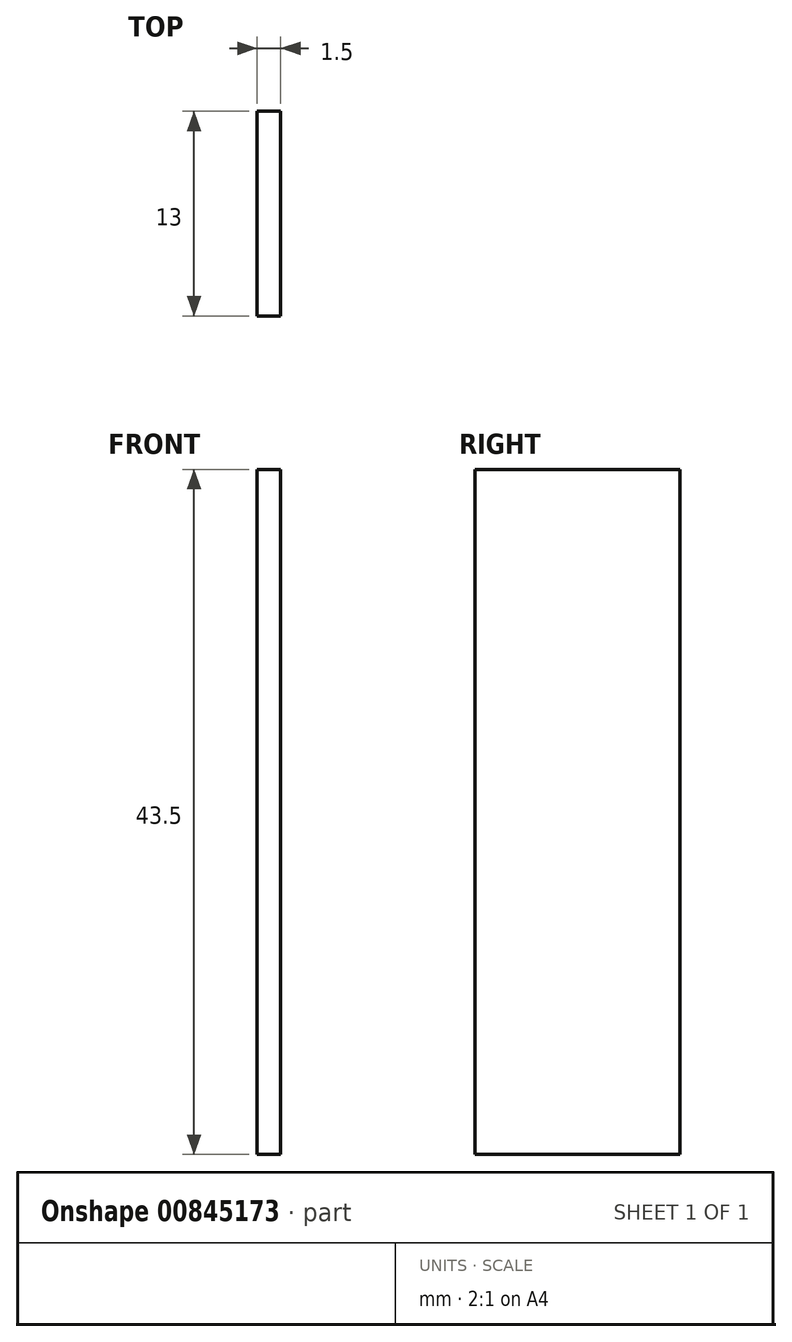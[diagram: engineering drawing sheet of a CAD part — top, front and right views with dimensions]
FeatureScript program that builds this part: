
annotation { "Feature Type Name" : "Feature", "Feature Type Description" : "" }
export const myFeature = defineFeature(function(context is Context, id is Id, definition is map)
    precondition{}
    {
        {
            var Q0;
            Q0=qCreatedBy(makeId("Right.planeOp"),FACE);
            var sketch = newSketch(context, id + "F0", { "sketchPlane" : qUnion([Q0])});
            skLineSegment(sketch, "E0.bottom", {"start": v(-6.5, -21.75) * mm, "end": v(6.5, -21.75) * mm});
            skLineSegment(sketch, "E0.top", {"start": v(-6.5, 21.75) * mm, "end": v(6.5, 21.75) * mm});
            skLineSegment(sketch, "E0.left", {"start": v(-6.5, -21.75) * mm, "end": v(-6.5, 21.75) * mm});
            skLineSegment(sketch, "E0.right", {"start": v(6.5, -21.75) * mm, "end": v(6.5, 21.75) * mm});
            skPoint(sketch, "E0.middle", {"position": v(0, 0) * mm});
            skSolve(sketch);
        }
        {
            var Q0;
            Q0=makeQuery(id+"F0.imprint","IMPRINT",FACE,{"disambiguationData":[TD([[makeQuery(id+"F0.imprint","IMPRINT",EDGE,{"derivedFrom":sQuery(id+"F0.wireOp",EDGE,"E0.bottom")}),1.0]])]});
            extrude(context, id + "F1", {"entities" : qUnion([Q0]), "depth" : 1.5 * mm, "offsetDistance" : 25 * mm});
        }
    });
